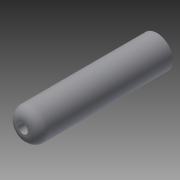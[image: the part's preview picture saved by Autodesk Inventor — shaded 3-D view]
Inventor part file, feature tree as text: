
AUTODESK INVENTOR PART (.ipt)
format: ipt  version: 2013 (Build 170138000, 138)  size: 88,064 bytes
history: native  units: in
note: dims shown in document units (in); Inventor stores cm internally (conversion verified against a paired STEP export)
features: extrude x1, fillet x1, sketch x1
ambient origin geometry x8: Origin, YZ Plane, XZ Plane, XY Plane, X Axis, Y Axis, Z Axis, Center Point
bodies: Solid1 (feature_tree)
feature tree (3):
  extrude  "Extrusion1"  Depth=0.75in
  fillet  "Fillet1"  Radius=10.5in
  sketch  "Sketch1"  dims[d0=2.5in d1=0.75in d2=10.5in d3=0.0in d4=0.75in]
